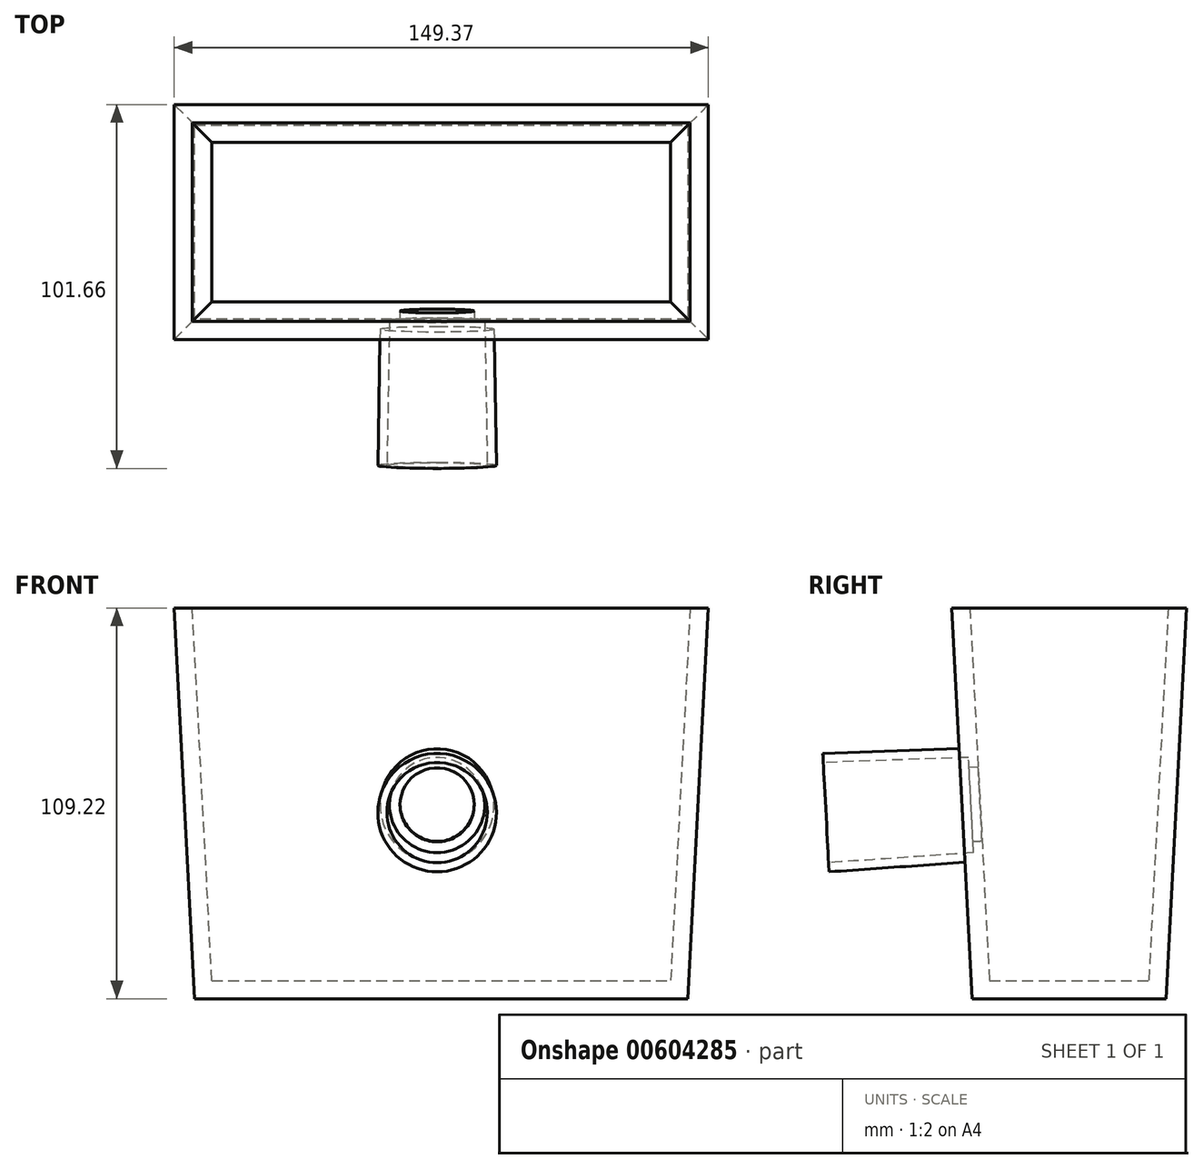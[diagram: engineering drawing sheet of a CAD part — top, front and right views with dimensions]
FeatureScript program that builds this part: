
annotation { "Feature Type Name" : "Feature", "Feature Type Description" : "" }
export const myFeature = defineFeature(function(context is Context, id is Id, definition is map)
    precondition{}
    {
        {
            var Q0;
            Q0=qCreatedBy(makeId("Top.planeOp"),FACE);
            var sketch = newSketch(context, id + "F0", { "sketchPlane" : qUnion([Q0])});
            skLineSegment(sketch, "E0.bottom", {"start": v(-67.8, 24.3) * mm, "end": v(70.13, 24.3) * mm});
            skLineSegment(sketch, "E0.top", {"start": v(-67.8, -29.89) * mm, "end": v(70.13, -29.89) * mm});
            skLineSegment(sketch, "E0.left", {"start": v(-67.8, 24.3) * mm, "end": v(-67.8, -29.89) * mm});
            skLineSegment(sketch, "E0.right", {"start": v(70.13, 24.3) * mm, "end": v(70.13, -29.89) * mm});
            skSolve(sketch);
        }
        {
            var Q0;
            Q0=makeQuery(id+"F0.imprint","IMPRINT",FACE,{"disambiguationData":[TD([[makeQuery(id+"F0.imprint","IMPRINT",EDGE,{"derivedFrom":sQuery(id+"F0.wireOp",EDGE,"E0.bottom")}),-1.0]])]});
            extrude(context, id + "F1", {"entities" : qUnion([Q0]), "depth" : 109.22 * mm, "offsetDistance" : 25.4 * mm, "hasDraft" : true, "draftAngle" : 3 * degree});
        }
        {
            var Q0;
            Q0=makeQuery(id+"F1.opExtrude","CAP_FACE",FACE,{"disambiguationData":[OSD([sQuery(id+"F0.wireOp",EDGE,"E0.bottom"),sQuery(id+"F0.wireOp",EDGE,"E0.top"),sQuery(id+"F0.wireOp",EDGE,"E0.left"),sQuery(id+"F0.wireOp",EDGE,"E0.right")])],"isStart":false});
            var Q1;
            Q1=makeQuery(id+"F1.opExtrude","SWEPT_BODY",BODY,{"disambiguationData":[OSD([sQuery(id+"F0.wireOp",EDGE,"E0.bottom"),sQuery(id+"F0.wireOp",EDGE,"E0.top"),sQuery(id+"F0.wireOp",EDGE,"E0.left"),sQuery(id+"F0.wireOp",EDGE,"E0.right")])]});
            shell(context, id + "F2", {"entities" : qUnion([Q0]), "parts" : qUnion([Q1]), "thickness" : 5.08 * mm});
        }
        {
            var Q0;
            Q0=makeQuery(id+"F1.opExtrude","SWEPT_FACE",FACE,{"disambiguationData":[OSD([sQuery(id+"F0.wireOp",EDGE,"E0.top")])]});
            var sketch = newSketch(context, id + "F3", { "sketchPlane" : qUnion([Q0])});
            skCircle(sketch, "E1", {"center": v(0, 55.64) * mm, "radius": 15.9 * mm});
            skSolve(sketch);
        }
        {
            var Q0;
            Q0 = qSketchRegion(id + "F3", true);
            extrude(context, id + "F4", {"entities" : qUnion([Q0]), "operationType" : NewBodyOperationType.ADD, "depth" : 38.1 * mm, "offsetDistance" : 25.4 * mm, "hasDraft" : true, "draftAngle" : 1 * degree});
        }
        {
            var Q0;
            Q0=makeQuery(id+"F4.opExtrude","CAP_FACE",FACE,{"disambiguationData":[OSD([sQuery(id+"F3.wireOp",EDGE,"E1")])],"isStart":false});
            shell(context, id + "F5", {"entities" : qUnion([Q0]), "thickness" : 2.54 * mm});
        }
        {
            var Q0;
            Q0=makeQuery(id+"F3.imprint","IMPRINT",FACE,{"disambiguationData":[TD([[makeQuery(id+"F3.imprint","IMPRINT",EDGE,{"derivedFrom":sQuery(id+"F3.wireOp",EDGE,"E1")}),1.0]])]});
            var sketch = newSketch(context, id + "F6", { "sketchPlane" : qUnion([Q0])});
            skCircle(sketch, "E2", {"center": v(0, 55.7) * mm, "radius": 10.36 * mm});
            skSolve(sketch);
        }
        {
            var Q0;
            Q0=makeQuery(id+"F6.imprint","IMPRINT",FACE,{"disambiguationData":[TD([[makeQuery(id+"F6.imprint","IMPRINT",EDGE,{"derivedFrom":sQuery(id+"F6.wireOp",EDGE,"E2")}),1.0]])]});
            extrude(context, id + "F7", {"entities" : qUnion([Q0]), "operationType" : NewBodyOperationType.REMOVE, "oppositeDirection" : true, "depth" : 28.2 * mm, "offsetDistance" : 25.4 * mm, "hasSecondDirection" : true, "secondDirectionOppositeDirection" : false, "secondDirectionDepth" : 25.4 * mm});
        }
    });
